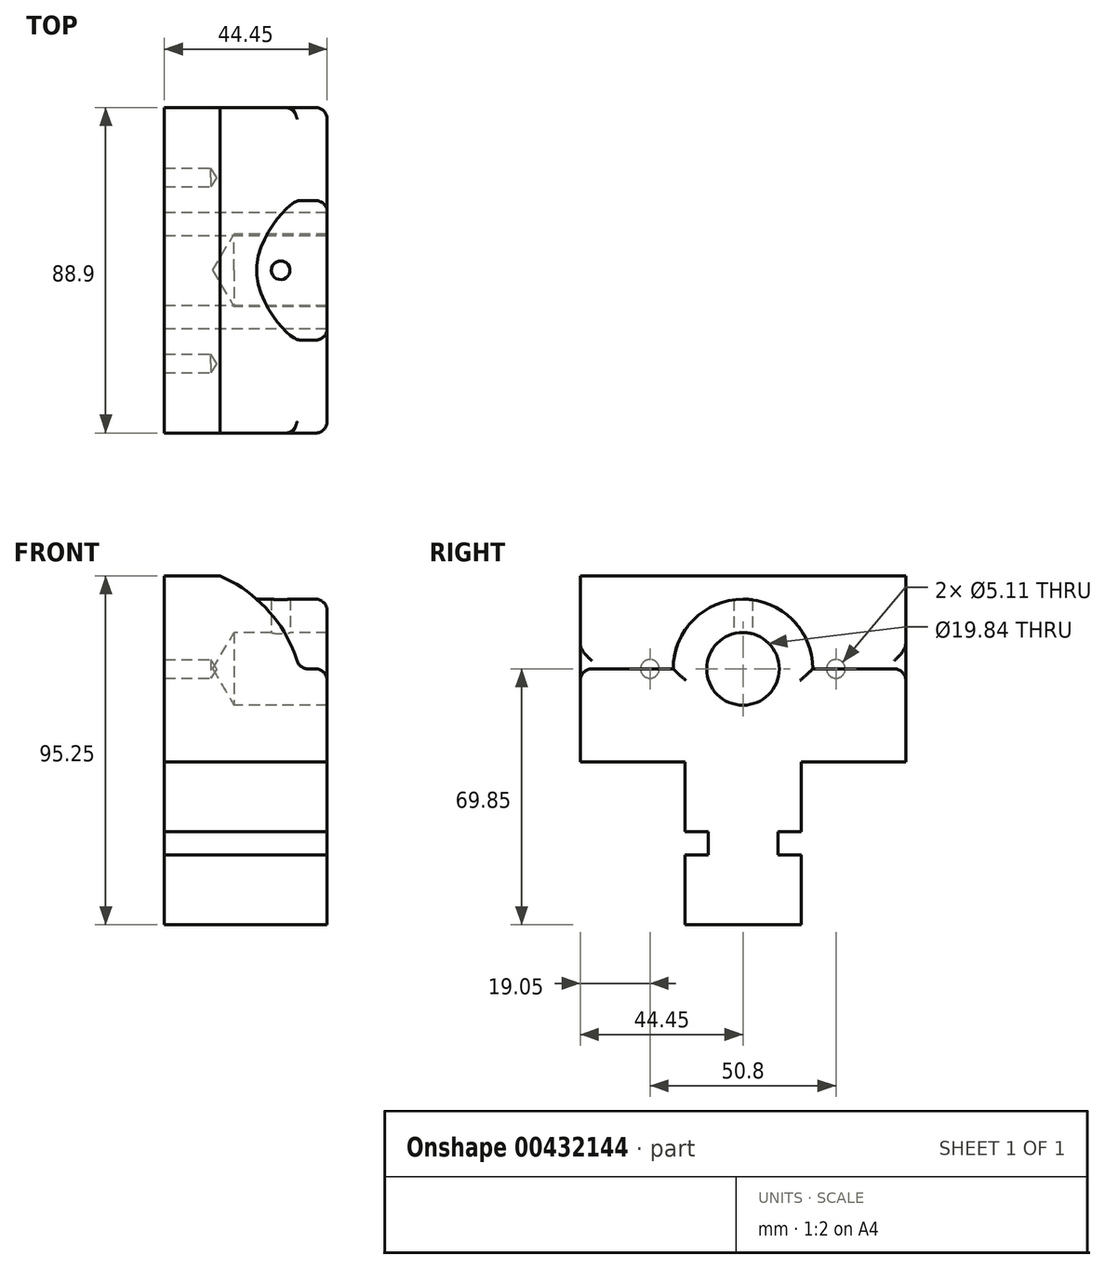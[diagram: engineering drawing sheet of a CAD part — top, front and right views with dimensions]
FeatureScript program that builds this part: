
annotation { "Feature Type Name" : "Feature", "Feature Type Description" : "" }
export const myFeature = defineFeature(function(context is Context, id is Id, definition is map)
    precondition{}
    {
        {
            var Q0;
            Q0=qCreatedBy(makeId("Front.planeOp"),FACE);
            var sketch = newSketch(context, id + "F0", { "sketchPlane" : qUnion([Q0])});
            skLineSegment(sketch, "E0", {"start": v(0, 0) * mm, "end": v(0, 50.8) * mm});
            skLineSegment(sketch, "E1", {"start": v(0, 50.8) * mm, "end": v(15.23, 50.8) * mm});
            skLineSegment(sketch, "E2", {"start": v(44.45, 0) * mm, "end": v(44.45, 25.4) * mm});
            skLineSegment(sketch, "E3", {"start": v(44.45, 25.4) * mm, "end": v(36.9, 25.4) * mm});
            skArc(sketch, "E4", {"start": v(36.9, 25.4) * mm, "mid": v(28.99, 40.6) * mm, "end": v(15.23, 50.8) * mm});
            skLineSegment(sketch, "E5", {"start": v(0, 0) * mm, "end": v(44.45, 0) * mm});
            skSolve(sketch);
        }
        {
            var Q0;
            Q0=makeQuery(id+"F0.imprint","IMPRINT",FACE,{"disambiguationData":[TD([[makeQuery(id+"F0.imprint","IMPRINT",EDGE,{"derivedFrom":sQuery(id+"F0.wireOp",EDGE,"E0")}),-1.0]])]});
            extrude(context, id + "F1", {"entities" : qUnion([Q0]), "depth" : 88.9 * mm, "symmetric" : true});
        }
        {
            var Q0;
            Q0=qCreatedBy(makeId("Front.planeOp"),FACE);
            var sketch = newSketch(context, id + "F2", { "sketchPlane" : qUnion([Q0])});
            skLineSegment(sketch, "E6.bottom", {"start": v(0, 0) * mm, "end": v(44.45, 0) * mm});
            skLineSegment(sketch, "E6.top", {"start": v(0, -44.45) * mm, "end": v(44.45, -44.45) * mm});
            skLineSegment(sketch, "E6.left", {"start": v(0, 0) * mm, "end": v(0, -44.45) * mm});
            skLineSegment(sketch, "E6.right", {"start": v(44.45, 0) * mm, "end": v(44.45, -44.45) * mm});
            skSolve(sketch);
        }
        {
            var Q0;
            Q0=makeQuery(id+"F2.imprint","IMPRINT",FACE,{"disambiguationData":[TD([[makeQuery(id+"F2.imprint","IMPRINT",EDGE,{"derivedFrom":sQuery(id+"F2.wireOp",EDGE,"E6.bottom")}),-1.0]])]});
            extrude(context, id + "F3", {"entities" : qUnion([Q0]), "operationType" : NewBodyOperationType.ADD, "depth" : 31.75 * mm, "symmetric" : true});
        }
        {
            var Q0;
            Q0=makeQuery(id+"F3.boolean.opBoolean","MERGE",FACE,{"derivedFrom":[makeQuery(id+"F1.opExtrude","SWEPT_FACE",FACE,{"disambiguationData":[OSD([sQuery(id+"F0.wireOp",EDGE,"E2")])]}),makeQuery(id+"F3.opExtrude","SWEPT_FACE",FACE,{"disambiguationData":[OSD([sQuery(id+"F2.wireOp",EDGE,"E6.right")])]})]});
            var sketch = newSketch(context, id + "F4", { "sketchPlane" : qUnion([Q0])});
            skCircle(sketch, "E7", {"center": v(0, 25.4) * mm, "radius": 19.05 * mm});
            skLineSegment(sketch, "E8.bottom", {"start": v(-15.88, -25.4) * mm, "end": v(-9.53, -25.4) * mm});
            skLineSegment(sketch, "E8.top", {"start": v(-15.88, -19.05) * mm, "end": v(-9.53, -19.05) * mm});
            skLineSegment(sketch, "E8.left", {"start": v(-15.88, -25.4) * mm, "end": v(-15.88, -19.05) * mm});
            skLineSegment(sketch, "E8.right", {"start": v(-9.53, -25.4) * mm, "end": v(-9.53, -19.05) * mm});
            skLineSegment(sketch, "E9.MirrorCS", {"start": v(15.88, -25.4) * mm, "end": v(15.88, -19.05) * mm});
            skLineSegment(sketch, "E10.MirrorCS", {"start": v(15.88, -19.05) * mm, "end": v(9.53, -19.05) * mm});
            skLineSegment(sketch, "E11.MirrorCS", {"start": v(9.53, -25.4) * mm, "end": v(9.53, -19.05) * mm});
            skLineSegment(sketch, "E12.MirrorCS", {"start": v(15.88, -25.4) * mm, "end": v(9.53, -25.4) * mm});
            skSolve(sketch);
        }
        {
            var Q0;
            {var subQ0=sQuery(id+"F4.wireOp",EDGE,"E7");var subQ1=makeQuery(id+"F1.opExtrude","SWEPT_EDGE",EDGE,{"disambiguationData":[OSD([sQuery(id+"F0.wireOp",EDGE,"E2"),sQuery(id+"F0.wireOp",EDGE,"E3")])]});var subQ2=makeQuery(id+"F4.imprint","INTERSECT",VERTEX,{"disambiguationData":[OD(0.0)],"derivedFrom":[subQ1,subQ0]});Q0=makeQuery(id+"F4.imprint","IMPRINT",FACE,{"disambiguationData":[TD([[makeQuery(id+"F4.imprint","IMPRINT",EDGE,{"disambiguationData":[TD([[subQ2,-1.0]])],"derivedFrom":subQ0}),1.0]])]});}
            extrude(context, id + "F5", {"entities" : qUnion([Q0]), "operationType" : NewBodyOperationType.ADD, "endBound" : BoundingType.UP_TO_NEXT, "oppositeDirection" : true, "depth" : 25.4 * mm});
        }
        {
            var Q0;
            Q0=makeQuery(id+"F4.imprint","IMPRINT",FACE,{"disambiguationData":[TD([[makeQuery(id+"F4.imprint","IMPRINT",EDGE,{"derivedFrom":sQuery(id+"F4.wireOp",EDGE,"E8.bottom")}),1.0]])]});
            var Q1;
            Q1=makeQuery(id+"F4.imprint","IMPRINT",FACE,{"disambiguationData":[TD([[makeQuery(id+"F4.imprint","IMPRINT",EDGE,{"derivedFrom":sQuery(id+"F4.wireOp",EDGE,"E9.MirrorCS")}),-1.0]])]});
            extrude(context, id + "F6", {"entities" : qUnion([Q0, Q1]), "operationType" : NewBodyOperationType.REMOVE, "endBound" : BoundingType.THROUGH_ALL, "oppositeDirection" : true, "depth" : 25.4 * mm});
        }
        {
            var Q0;
            Q0=sQuery(id+"F4.wireOp",VERTEX,"E7.center");
            var Q1;
            Q1=makeQuery(id+"F1.opExtrude","SWEPT_BODY",BODY,{"disambiguationData":[OSD([sQuery(id+"F0.wireOp",EDGE,"E0"),sQuery(id+"F0.wireOp",EDGE,"E1"),sQuery(id+"F0.wireOp",EDGE,"E2"),sQuery(id+"F0.wireOp",EDGE,"E3"),sQuery(id+"F0.wireOp",EDGE,"E4"),sQuery(id+"F0.wireOp",EDGE,"E5")])]});
            hole(context, id + "F7", {"style" : HoleStyle.SIMPLE, "endStyle" : HoleEndStyle.BLIND, "standardTappedOrClearance" : lookupTablePath({ "standard" : "ANSI", "fit" : "Normal (ASME)", "size" : "3/4", "type" : "Clearance" }), "standardBlindInLast" : lookupTablePath({ "fit" : "Free", "standard" : "ANSI", "size" : "3/4", "type" : "Clearance" }), "holeDiameter" : 19.84 * mm, "holeDepth" : 25.4 * mm, "isTappedThrough" : true, "tappedDepth" : 12.7 * mm, "tapClearance" : 3, "locations" : qUnion([Q0]), "scope" : qUnion([Q1]), "startStyle" : HoleStartStyle.SKETCH});
        }
        {
            var Q0;
            {var subQ0=sQuery(id+"F0.wireOp",EDGE,"E4");var subQ1=sQuery(id+"F0.wireOp",EDGE,"E3");Q0=makeQuery(id+"F5.boolean.opBoolean","SPLIT",EDGE,{"disambiguationData":[TD([makeQuery(id+"F1.opExtrude","CAP_FACE",FACE,{"disambiguationData":[OSD([sQuery(id+"F0.wireOp",EDGE,"E0"),sQuery(id+"F0.wireOp",EDGE,"E1"),sQuery(id+"F0.wireOp",EDGE,"E2"),subQ1,subQ0,sQuery(id+"F0.wireOp",EDGE,"E5")])],"isStart":false})])],"derivedFrom":makeQuery(id+"F1.opExtrude","SWEPT_EDGE",EDGE,{"disambiguationData":[OSD([subQ1,subQ0])]})});}
            var Q1;
            {var subQ0=sQuery(id+"F0.wireOp",EDGE,"E4");var subQ1=sQuery(id+"F0.wireOp",EDGE,"E3");Q1=makeQuery(id+"F5.boolean.opBoolean","SPLIT",EDGE,{"disambiguationData":[TD([makeQuery(id+"F1.opExtrude","CAP_FACE",FACE,{"disambiguationData":[OSD([sQuery(id+"F0.wireOp",EDGE,"E0"),sQuery(id+"F0.wireOp",EDGE,"E1"),sQuery(id+"F0.wireOp",EDGE,"E2"),subQ1,subQ0,sQuery(id+"F0.wireOp",EDGE,"E5")])],"isStart":true})])],"derivedFrom":makeQuery(id+"F1.opExtrude","SWEPT_EDGE",EDGE,{"disambiguationData":[OSD([subQ1,subQ0])]})});}
            var Q2;
            {var subQ0=sQuery(id+"F4.wireOp",EDGE,"E7");var subQ1=makeQuery(id+"F1.opExtrude","SWEPT_EDGE",EDGE,{"disambiguationData":[OSD([sQuery(id+"F0.wireOp",EDGE,"E2"),sQuery(id+"F0.wireOp",EDGE,"E3")])]});Q2=makeQuery(id+"F5.opExtrude","TWEAK_EDGE",EDGE,{"derivedFrom":[makeQuery(id+"F1.opExtrude","SWEPT_FACE",FACE,{"disambiguationData":[OSD([sQuery(id+"F0.wireOp",EDGE,"E4")])]}),makeQuery(id+"F4.imprint","IMPRINT",EDGE,{"disambiguationData":[TD([[makeQuery(id+"F4.imprint","INTERSECT",VERTEX,{"disambiguationData":[OD(0.0)],"derivedFrom":[subQ1,subQ0]}),-1.0]])],"derivedFrom":subQ0})]});}
            var Q3;
            Q3=makeQuery(id+"F1.opExtrude","CAP_EDGE",EDGE,{"disambiguationData":[OSD([sQuery(id+"F0.wireOp",EDGE,"E2")])],"isStart":true});
            var Q4;
            Q4=makeQuery(id+"F1.opExtrude","CAP_EDGE",EDGE,{"disambiguationData":[OSD([sQuery(id+"F0.wireOp",EDGE,"E2")])],"isStart":false});
            var Q5;
            {var subQ0=sQuery(id+"F0.wireOp",EDGE,"E3");var subQ1=sQuery(id+"F0.wireOp",EDGE,"E2");Q5=makeQuery(id+"F5.boolean.opBoolean","SPLIT",EDGE,{"disambiguationData":[TD([makeQuery(id+"F1.opExtrude","CAP_FACE",FACE,{"disambiguationData":[OSD([sQuery(id+"F0.wireOp",EDGE,"E0"),sQuery(id+"F0.wireOp",EDGE,"E1"),subQ1,subQ0,sQuery(id+"F0.wireOp",EDGE,"E4"),sQuery(id+"F0.wireOp",EDGE,"E5")])],"isStart":false})])],"derivedFrom":makeQuery(id+"F1.opExtrude","SWEPT_EDGE",EDGE,{"disambiguationData":[OSD([subQ1,subQ0])]})});}
            var Q6;
            Q6=makeQuery(id+"F1.opExtrude","CAP_EDGE",EDGE,{"disambiguationData":[OSD([sQuery(id+"F0.wireOp",EDGE,"E3")])],"isStart":false});
            var Q7;
            Q7=makeQuery(id+"F5.opExtrude","CAP_EDGE",EDGE,{"disambiguationData":[OSD([sQuery(id+"F4.wireOp",EDGE,"E7")])],"isStart":true});
            var Q8;
            {var subQ0=sQuery(id+"F4.wireOp",EDGE,"E7");var subQ1=sQuery(id+"F0.wireOp",EDGE,"E3");var subQ2=sQuery(id+"F0.wireOp",EDGE,"E2");Q8=makeQuery(id+"F5.opExtrude","SWEPT_EDGE",EDGE,{"disambiguationData":[OSD([subQ2,subQ1,subQ0]),TDD([makeQuery(id+"F4.imprint","INTERSECT",VERTEX,{"disambiguationData":[OD(0.0)],"derivedFrom":[makeQuery(id+"F1.opExtrude","SWEPT_EDGE",EDGE,{"disambiguationData":[OSD([subQ2,subQ1])]}),subQ0]})])]});}
            var Q9;
            {var subQ0=sQuery(id+"F0.wireOp",EDGE,"E3");var subQ1=sQuery(id+"F0.wireOp",EDGE,"E2");Q9=makeQuery(id+"F5.boolean.opBoolean","SPLIT",EDGE,{"disambiguationData":[TD([makeQuery(id+"F1.opExtrude","CAP_FACE",FACE,{"disambiguationData":[OSD([sQuery(id+"F0.wireOp",EDGE,"E0"),sQuery(id+"F0.wireOp",EDGE,"E1"),subQ1,subQ0,sQuery(id+"F0.wireOp",EDGE,"E4"),sQuery(id+"F0.wireOp",EDGE,"E5")])],"isStart":true})])],"derivedFrom":makeQuery(id+"F1.opExtrude","SWEPT_EDGE",EDGE,{"disambiguationData":[OSD([subQ1,subQ0])]})});}
            var Q10;
            Q10=makeQuery(id+"F1.opExtrude","CAP_EDGE",EDGE,{"disambiguationData":[OSD([sQuery(id+"F0.wireOp",EDGE,"E3")])],"isStart":true});
            var Q11;
            {var subQ0=sQuery(id+"F4.wireOp",EDGE,"E7");var subQ1=sQuery(id+"F0.wireOp",EDGE,"E3");var subQ2=sQuery(id+"F0.wireOp",EDGE,"E2");Q11=makeQuery(id+"F5.opExtrude","SWEPT_EDGE",EDGE,{"disambiguationData":[OSD([subQ2,subQ1,subQ0]),TDD([makeQuery(id+"F4.imprint","INTERSECT",VERTEX,{"disambiguationData":[OD(1.0)],"derivedFrom":[makeQuery(id+"F1.opExtrude","SWEPT_EDGE",EDGE,{"disambiguationData":[OSD([subQ2,subQ1])]}),subQ0]})])]});}
            fillet(context, id + "F8", {"entities" : qUnion([Q0, Q1, Q2, Q3, Q4, Q5, Q6, Q7, Q8, Q9, Q10, Q11]), "radius" : 3.17 * mm, "tangentPropagation" : true, "allowEdgeOverflow" : false});
        }
        {
            var Q0;
            Q0=qCreatedBy(makeId("Top.planeOp"),FACE);
            cPlane(context, id + "F9", {"entities" : qUnion([Q0]), "cplaneType" : CPlaneType.OFFSET, "offset" : 44.45 * mm, "width" : 152.4 * mm, "height" : 152.4 * mm});
        }
        {
            var Q0;
            Q0=qCreatedBy(id+"F9.planeOp",FACE);
            var sketch = newSketch(context, id + "F10", { "sketchPlane" : qUnion([Q0])});
            skPoint(sketch, "E13", {"position": v(31.75, 0) * mm});
            skSolve(sketch);
        }
        {
            var Q0;
            Q0=sQuery(id+"F10.wireOp",VERTEX,"E13");
            var Q1;
            Q1=makeQuery(id+"F1.opExtrude","SWEPT_BODY",BODY,{"disambiguationData":[OSD([sQuery(id+"F0.wireOp",EDGE,"E0"),sQuery(id+"F0.wireOp",EDGE,"E1"),sQuery(id+"F0.wireOp",EDGE,"E2"),sQuery(id+"F0.wireOp",EDGE,"E3"),sQuery(id+"F0.wireOp",EDGE,"E4"),sQuery(id+"F0.wireOp",EDGE,"E5")])]});
            hole(context, id + "F11", {"style" : HoleStyle.SIMPLE, "endStyle" : HoleEndStyle.BLIND, "standardTappedOrClearance" : lookupTablePath({ "standard" : "ANSI", "engagement" : "75%", "pitch" : "20 tpi", "size" : "1/4", "type" : "Tapped" }), "standardBlindInLast" : lookupTablePath({ "standard" : "ANSI", "engagement" : "75%", "pitch" : "20 tpi", "size" : "1/4", "type" : "Tapped" }), "holeDiameter" : 5.1 * mm, "showTappedDepth" : true, "holeDepth" : 16.51 * mm, "isTappedThrough" : true, "tappedDepth" : 12.7 * mm, "tapClearance" : 3, "locations" : qUnion([Q0]), "scope" : qUnion([Q1]), "majorDiameter" : 6.35 * mm, "startStyle" : HoleStartStyle.SKETCH});
        }
        {
            var Q0;
            Q0=makeQuery(id+"F3.boolean.opBoolean","MERGE",FACE,{"derivedFrom":[makeQuery(id+"F1.opExtrude","SWEPT_FACE",FACE,{"disambiguationData":[OSD([sQuery(id+"F0.wireOp",EDGE,"E0")])]}),makeQuery(id+"F3.opExtrude","SWEPT_FACE",FACE,{"disambiguationData":[OSD([sQuery(id+"F2.wireOp",EDGE,"E6.left")])]})]});
            var sketch = newSketch(context, id + "F12", { "sketchPlane" : qUnion([Q0])});
            skPoint(sketch, "E14", {"position": v(-25.4, 25.4) * mm});
            skPoint(sketch, "E14.positionSnap0", {"position": v(-44.45, 25.4) * mm});
            skPoint(sketch, "E15", {"position": v(25.4, 25.4) * mm});
            skPoint(sketch, "E15.positionSnap0", {"position": v(44.45, 25.4) * mm});
            skSolve(sketch);
        }
        {
            var Q0;
            Q0=sQuery(id+"F12.wireOp",VERTEX,"E14");
            var Q1;
            Q1=sQuery(id+"F12.wireOp",VERTEX,"E15");
            var Q2;
            Q2=makeQuery(id+"F1.opExtrude","SWEPT_BODY",BODY,{"disambiguationData":[OSD([sQuery(id+"F0.wireOp",EDGE,"E0"),sQuery(id+"F0.wireOp",EDGE,"E1"),sQuery(id+"F0.wireOp",EDGE,"E2"),sQuery(id+"F0.wireOp",EDGE,"E3"),sQuery(id+"F0.wireOp",EDGE,"E4"),sQuery(id+"F0.wireOp",EDGE,"E5")])]});
            hole(context, id + "F13", {"style" : HoleStyle.SIMPLE, "endStyle" : HoleEndStyle.BLIND, "standardTappedOrClearance" : lookupTablePath({ "standard" : "ANSI", "engagement" : "75%", "pitch" : "20 tpi", "size" : "1/4", "type" : "Tapped" }), "standardBlindInLast" : lookupTablePath({ "standard" : "ANSI", "engagement" : "75%", "pitch" : "20 tpi", "size" : "1/4", "type" : "Tapped" }), "holeDiameter" : 5.1 * mm, "showTappedDepth" : true, "holeDepth" : 12.7 * mm, "tappedDepth" : 8.9 * mm, "tapClearance" : 3, "locations" : qUnion([Q0, Q1]), "scope" : qUnion([Q2]), "majorDiameter" : 6.35 * mm, "startStyle" : HoleStartStyle.SKETCH});
        }
    });
